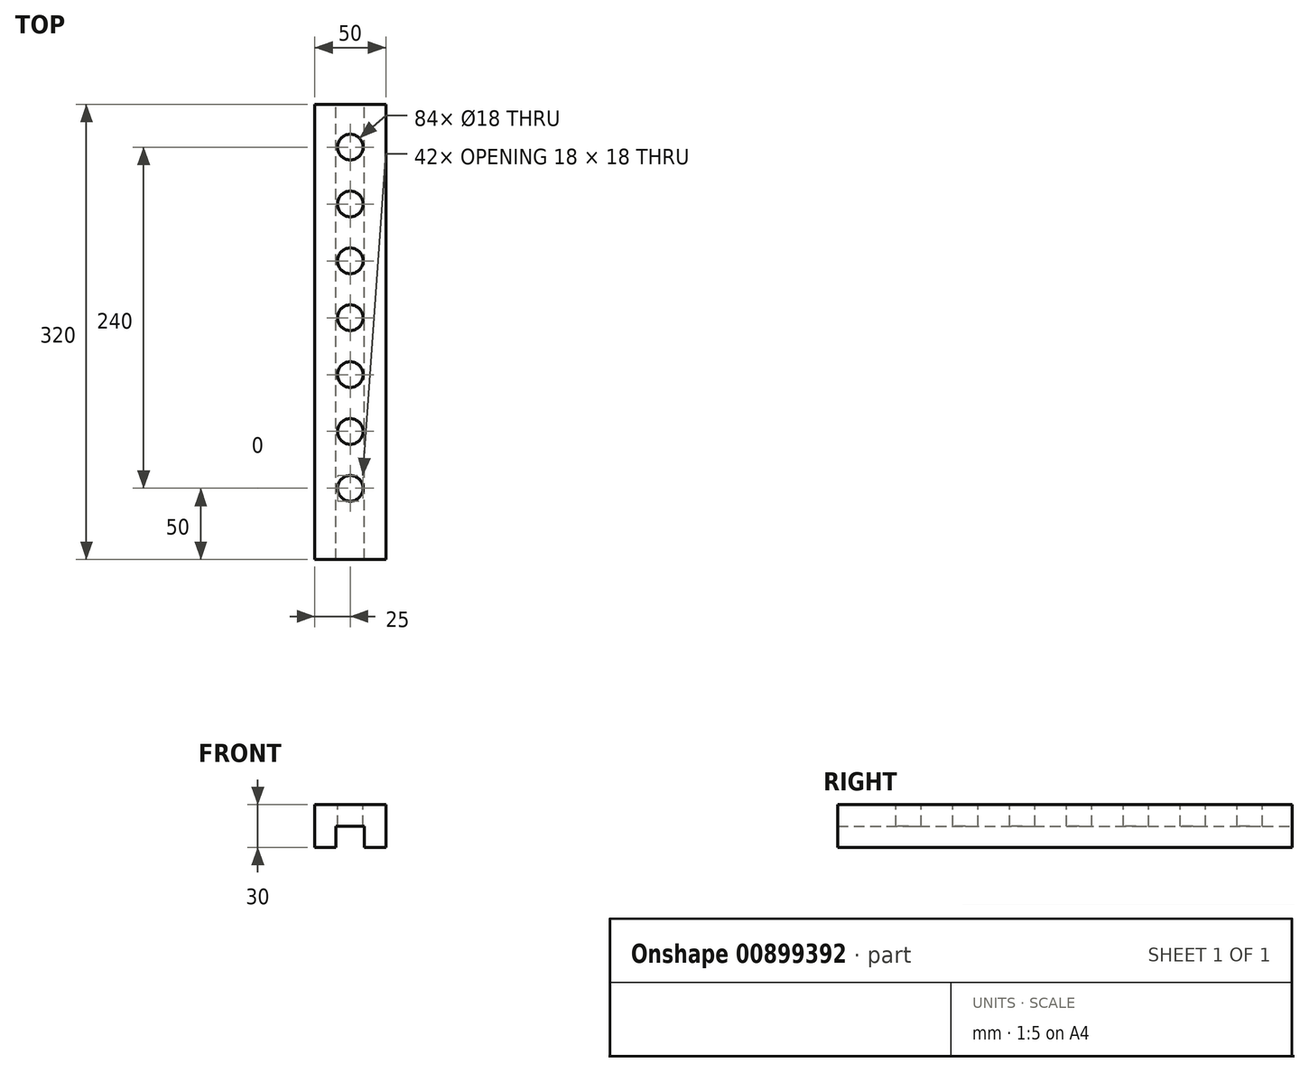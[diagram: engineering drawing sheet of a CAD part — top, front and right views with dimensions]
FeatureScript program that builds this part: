
annotation { "Feature Type Name" : "Feature", "Feature Type Description" : "" }
export const myFeature = defineFeature(function(context is Context, id is Id, definition is map)
    precondition{}
    {
        {
            var Q0;
            Q0=qCreatedBy(makeId("Top.planeOp"),FACE);
            var sketch = newSketch(context, id + "F0", { "sketchPlane" : qUnion([Q0])});
            skLineSegment(sketch, "E0.bottom", {"start": v(0, 0) * mm, "end": v(50, 0) * mm});
            skLineSegment(sketch, "E0.top", {"start": v(0, 320) * mm, "end": v(50, 320) * mm});
            skLineSegment(sketch, "E0.left", {"start": v(0, 0) * mm, "end": v(0, 320) * mm});
            skLineSegment(sketch, "E0.right", {"start": v(50, 0) * mm, "end": v(50, 320) * mm});
            skSolve(sketch);
        }
        {
            var Q0;
            Q0 = qSketchRegion(id + "F0", true);
            extrude(context, id + "F1", {"entities" : qUnion([Q0]), "depth" : 30 * mm, "offsetDistance" : 25 * mm});
        }
        {
            var Q0;
            Q0=makeQuery(id+"F1.opExtrude","CAP_FACE",FACE,{"disambiguationData":[OSD([sQuery(id+"F0.wireOp",EDGE,"E0.bottom"),sQuery(id+"F0.wireOp",EDGE,"E0.top"),sQuery(id+"F0.wireOp",EDGE,"E0.left"),sQuery(id+"F0.wireOp",EDGE,"E0.right")])],"isStart":true});
            var sketch = newSketch(context, id + "F2", { "sketchPlane" : qUnion([Q0])});
            skLineSegment(sketch, "E1.bottom", {"start": v(15, 0) * mm, "end": v(35, 0) * mm});
            skLineSegment(sketch, "E1.top", {"start": v(15, -320) * mm, "end": v(35, -320) * mm});
            skLineSegment(sketch, "E1.left", {"start": v(15, 0) * mm, "end": v(15, -320) * mm});
            skLineSegment(sketch, "E1.right", {"start": v(35, 0) * mm, "end": v(35, -320) * mm});
            skSolve(sketch);
        }
        {
            var Q0;
            Q0 = qSketchRegion(id + "F2", true);
            extrude(context, id + "F3", {"entities" : qUnion([Q0]), "operationType" : NewBodyOperationType.REMOVE, "oppositeDirection" : true, "depth" : 15 * mm, "offsetDistance" : 25 * mm});
        }
        {
            var Q0;
            Q0=makeQuery(id+"F1.opExtrude","CAP_FACE",FACE,{"disambiguationData":[OSD([sQuery(id+"F0.wireOp",EDGE,"E0.bottom"),sQuery(id+"F0.wireOp",EDGE,"E0.top"),sQuery(id+"F0.wireOp",EDGE,"E0.left"),sQuery(id+"F0.wireOp",EDGE,"E0.right")])],"isStart":false});
            var sketch = newSketch(context, id + "F4", { "sketchPlane" : qUnion([Q0])});
            skCircle(sketch, "E2", {"center": v(25, 50) * mm, "radius": 9 * mm});
            skCircle(sketch, "E3.0.1.0", {"center": v(25, 90) * mm, "radius": 9 * mm});
            skCircle(sketch, "E3.0.2.0", {"center": v(25, 130) * mm, "radius": 9 * mm});
            skCircle(sketch, "E3.0.3.0", {"center": v(25, 170) * mm, "radius": 9 * mm});
            skCircle(sketch, "E3.0.4.0", {"center": v(25, 210) * mm, "radius": 9 * mm});
            skCircle(sketch, "E3.0.5.0", {"center": v(25, 250) * mm, "radius": 9 * mm});
            skCircle(sketch, "E3.0.6.0", {"center": v(25, 290) * mm, "radius": 9 * mm});
            skLineSegment(sketch, "E3.direction1", {"start": v(25, 50) * mm, "end": v(50, 50) * mm, "construction": true});
            skLineSegment(sketch, "E3.direction2", {"start": v(25, 50) * mm, "end": v(25, 90) * mm, "construction": true});
            skSolve(sketch);
        }
        {
            var Q0;
            Q0 = qSketchRegion(id + "F4", true);
            extrude(context, id + "F5", {"entities" : qUnion([Q0]), "operationType" : NewBodyOperationType.REMOVE, "endBound" : BoundingType.THROUGH_ALL, "oppositeDirection" : true, "depth" : 25 * mm, "offsetDistance" : 25 * mm});
        }
    });
